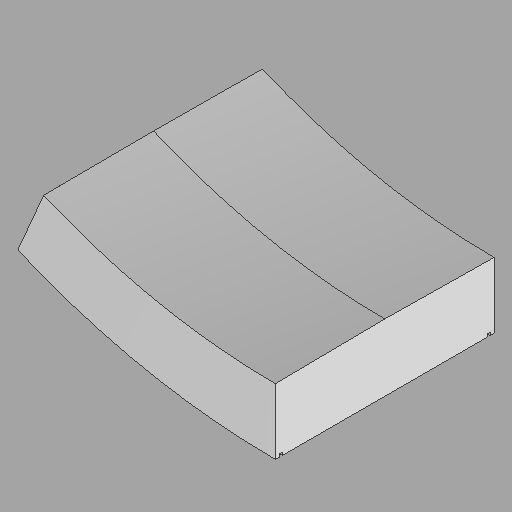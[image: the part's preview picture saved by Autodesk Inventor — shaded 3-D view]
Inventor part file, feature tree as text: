
AUTODESK INVENTOR PART (.ipt)
format: ipt  version: 2022.2 (Build 262287010, 287A)  size: 174,080 bytes
history: native  units: in
note: dims shown in document units (in); Inventor stores cm internally (conversion verified against a paired STEP export)
features: sketch x4, sweep x3, thicken_offset x1, projected_geometry x1, other x1
ambient origin geometry x8: Origin, YZ Plane, XZ Plane, XY Plane, X Axis, Y Axis, Z Axis, Center Point
bodies: Solid1 (feature_tree)
feature tree (10):
  thicken_offset  "Thicken1"
  sketch  "Sketch2"  dims[d0=11.0in d1=11.0in d9=0.125in d10=0.25in d11=0.25in d12=0.375in d13=0.25in d14=0.25in d15=0.375in d16=0.25in d17=0.25in d18=0.0in d19=0.0in d20=0.0in d21=0.0in d22=0.0in d23=0.0in]
  sweep  "Sweep1"
  sweep  "Sweep2"
  sweep  "Sweep3"
  projected_geometry  "Projected Loop2"
  sketch  "3D Sketch1"
  sketch  "3D Sketch2"
  sketch  "3D Sketch3"
  other  "Cap (5) (1)"
